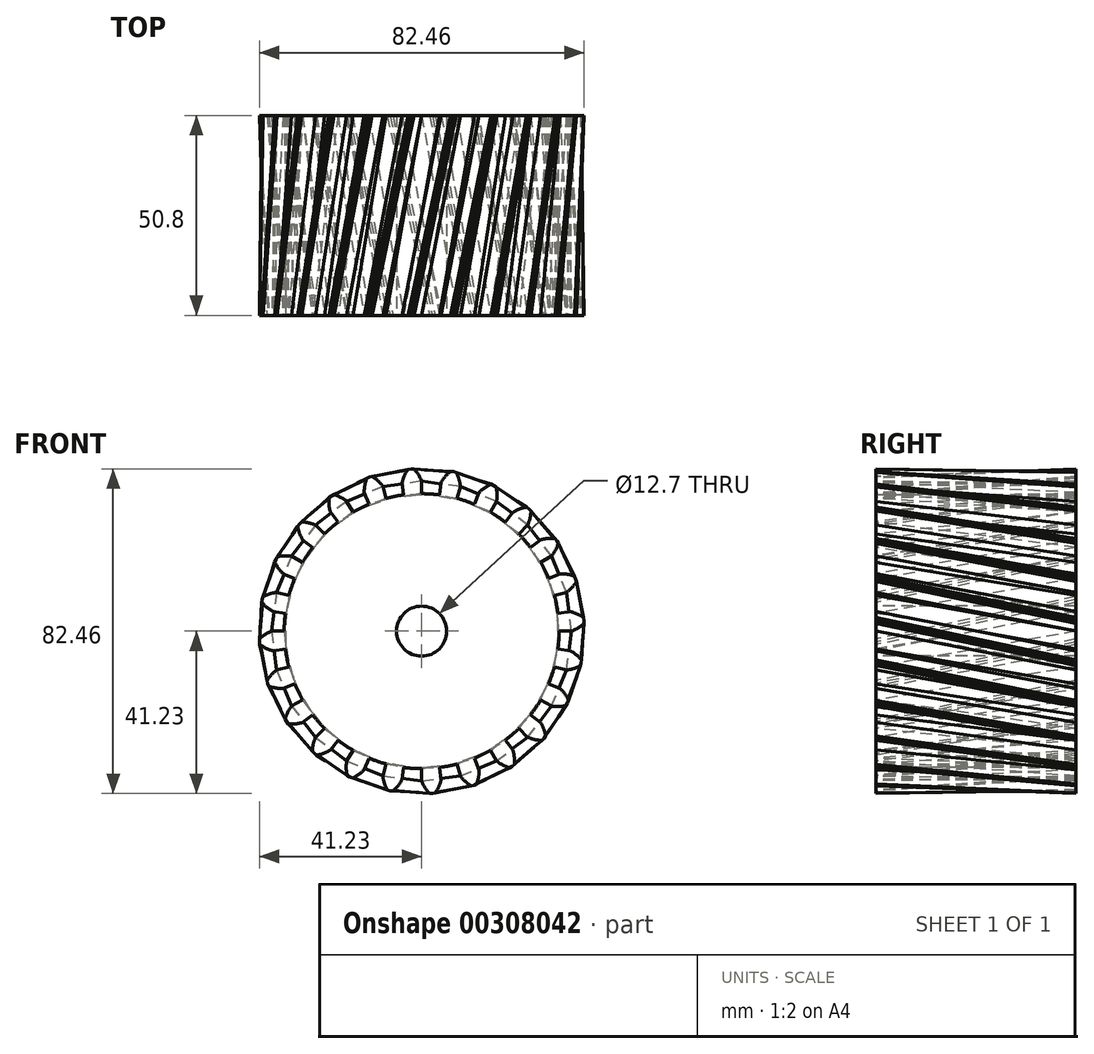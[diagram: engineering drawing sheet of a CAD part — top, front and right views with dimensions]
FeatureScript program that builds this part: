
annotation { "Feature Type Name" : "Feature", "Feature Type Description" : "" }
export const myFeature = defineFeature(function(context is Context, id is Id, definition is map)
    precondition{}
    {
        {
            var Q0;
            Q0=qCreatedBy(makeId("Front.planeOp"),FACE);
            var sketch = newSketch(context, id + "F0", { "sketchPlane" : qUnion([Q0])});
            skArc(sketch, "E0", {"start": v(-4.56, 34.63) * mm, "mid": v(-6.81, 34.25) * mm, "end": v(-9.04, 33.73) * mm});
            skArc(sketch, "E1.trimOffspring", {"start": v(0, 38.1) * mm, "mid": v(-0.83, 39.76) * mm, "end": v(-1.97, 41.23) * mm});
            skLineSegment(sketch, "E2", {"start": v(0, 38.1) * mm, "end": v(0, 34.93) * mm});
            skLineSegment(sketch, "E3", {"start": v(-1.97, 41.23) * mm, "end": v(-2.7, 41.23) * mm});
            skLineSegment(sketch, "E4.MirrorCS", {"start": v(-3.43, 41.13) * mm, "end": v(-2.7, 41.23) * mm});
            skArc(sketch, "E5.MirrorCS", {"start": v(-4.97, 37.77) * mm, "mid": v(-4.36, 39.53) * mm, "end": v(-3.43, 41.13) * mm});
            skLineSegment(sketch, "E6.MirrorCS", {"start": v(-4.97, 37.77) * mm, "end": v(-4.56, 34.63) * mm});
            skLineSegment(sketch, "E7.1.0", {"start": v(-14.58, 35.2) * mm, "end": v(-13.37, 32.27) * mm});
            skArc(sketch, "E7.1.1", {"start": v(-14.58, 35.2) * mm, "mid": v(-14.45, 37.05) * mm, "end": v(-13.96, 38.84) * mm});
            skLineSegment(sketch, "E7.1.2", {"start": v(-13.96, 38.84) * mm, "end": v(-13.28, 39.12) * mm});
            skLineSegment(sketch, "E7.1.3", {"start": v(-12.58, 39.31) * mm, "end": v(-13.28, 39.12) * mm});
            skLineSegment(sketch, "E7.1.4", {"start": v(-9.86, 36.8) * mm, "end": v(-9.04, 33.73) * mm});
            skArc(sketch, "E7.1.5", {"start": v(-9.86, 36.8) * mm, "mid": v(-11.1, 38.2) * mm, "end": v(-12.58, 39.31) * mm});
            skLineSegment(sketch, "E7.2.0", {"start": v(-23.2, 30.23) * mm, "end": v(-21.26, 27.7) * mm});
            skArc(sketch, "E7.2.1", {"start": v(-23.2, 30.23) * mm, "mid": v(-23.54, 32.05) * mm, "end": v(-23.53, 33.9) * mm});
            skLineSegment(sketch, "E7.2.2", {"start": v(-23.53, 33.9) * mm, "end": v(-22.95, 34.35) * mm});
            skLineSegment(sketch, "E7.2.3", {"start": v(-22.32, 34.72) * mm, "end": v(-22.95, 34.35) * mm});
            skLineSegment(sketch, "E7.2.4", {"start": v(-19.05, 33) * mm, "end": v(-17.46, 30.25) * mm});
            skArc(sketch, "E7.2.5", {"start": v(-19.05, 33) * mm, "mid": v(-20.6, 34.02) * mm, "end": v(-22.32, 34.72) * mm});
            skLineSegment(sketch, "E7.3.0", {"start": v(-30.23, 23.2) * mm, "end": v(-27.7, 21.26) * mm});
            skArc(sketch, "E7.3.1", {"start": v(-30.23, 23.2) * mm, "mid": v(-31.04, 24.87) * mm, "end": v(-31.5, 26.66) * mm});
            skLineSegment(sketch, "E7.3.2", {"start": v(-31.5, 26.66) * mm, "end": v(-31.06, 27.24) * mm});
            skLineSegment(sketch, "E7.3.3", {"start": v(-30.55, 27.76) * mm, "end": v(-31.06, 27.24) * mm});
            skLineSegment(sketch, "E7.3.4", {"start": v(-26.94, 26.94) * mm, "end": v(-24.7, 24.7) * mm});
            skArc(sketch, "E7.3.5", {"start": v(-26.94, 26.94) * mm, "mid": v(-28.7, 27.53) * mm, "end": v(-30.55, 27.76) * mm});
            skLineSegment(sketch, "E7.4.0", {"start": v(-35.2, 14.58) * mm, "end": v(-32.27, 13.37) * mm});
            skArc(sketch, "E7.4.1", {"start": v(-35.2, 14.58) * mm, "mid": v(-36.42, 15.99) * mm, "end": v(-37.33, 17.6) * mm});
            skLineSegment(sketch, "E7.4.2", {"start": v(-37.33, 17.6) * mm, "end": v(-37.06, 18.27) * mm});
            skLineSegment(sketch, "E7.4.3", {"start": v(-36.7, 18.9) * mm, "end": v(-37.06, 18.27) * mm});
            skLineSegment(sketch, "E7.4.4", {"start": v(-33, 19.05) * mm, "end": v(-30.25, 17.46) * mm});
            skArc(sketch, "E7.4.5", {"start": v(-33, 19.05) * mm, "mid": v(-34.85, 19.16) * mm, "end": v(-36.7, 18.9) * mm});
            skLineSegment(sketch, "E7.5.0", {"start": v(-37.77, 4.97) * mm, "end": v(-34.63, 4.56) * mm});
            skArc(sketch, "E7.5.1", {"start": v(-37.77, 4.97) * mm, "mid": v(-39.31, 6.02) * mm, "end": v(-40.62, 7.34) * mm});
            skLineSegment(sketch, "E7.5.2", {"start": v(-40.62, 7.34) * mm, "end": v(-40.52, 8.06) * mm});
            skLineSegment(sketch, "E7.5.3", {"start": v(-40.33, 8.77) * mm, "end": v(-40.52, 8.06) * mm});
            skLineSegment(sketch, "E7.5.4", {"start": v(-36.8, 9.86) * mm, "end": v(-33.73, 9.04) * mm});
            skArc(sketch, "E7.5.5", {"start": v(-36.8, 9.86) * mm, "mid": v(-38.62, 9.49) * mm, "end": v(-40.33, 8.77) * mm});
            skLineSegment(sketch, "E7.6.0", {"start": v(-37.77, -4.97) * mm, "end": v(-34.63, -4.56) * mm});
            skArc(sketch, "E7.6.1", {"start": v(-37.77, -4.97) * mm, "mid": v(-39.53, -4.36) * mm, "end": v(-41.13, -3.43) * mm});
            skLineSegment(sketch, "E7.6.2", {"start": v(-41.13, -3.43) * mm, "end": v(-41.23, -2.7) * mm});
            skLineSegment(sketch, "E7.6.3", {"start": v(-41.23, -1.97) * mm, "end": v(-41.23, -2.7) * mm});
            skLineSegment(sketch, "E7.6.4", {"start": v(-38.1, 0) * mm, "end": v(-34.93, 0) * mm});
            skArc(sketch, "E7.6.5", {"start": v(-38.1, 0) * mm, "mid": v(-39.76, -0.83) * mm, "end": v(-41.23, -1.97) * mm});
            skLineSegment(sketch, "E7.7.0", {"start": v(-35.2, -14.58) * mm, "end": v(-32.27, -13.37) * mm});
            skArc(sketch, "E7.7.1", {"start": v(-35.2, -14.58) * mm, "mid": v(-37.05, -14.45) * mm, "end": v(-38.84, -13.96) * mm});
            skLineSegment(sketch, "E7.7.2", {"start": v(-38.84, -13.96) * mm, "end": v(-39.12, -13.28) * mm});
            skLineSegment(sketch, "E7.7.3", {"start": v(-39.31, -12.58) * mm, "end": v(-39.12, -13.28) * mm});
            skLineSegment(sketch, "E7.7.4", {"start": v(-36.8, -9.86) * mm, "end": v(-33.73, -9.04) * mm});
            skArc(sketch, "E7.7.5", {"start": v(-36.8, -9.86) * mm, "mid": v(-38.2, -11.1) * mm, "end": v(-39.31, -12.58) * mm});
            skLineSegment(sketch, "E7.8.0", {"start": v(-30.23, -23.2) * mm, "end": v(-27.7, -21.26) * mm});
            skArc(sketch, "E7.8.1", {"start": v(-30.23, -23.2) * mm, "mid": v(-32.05, -23.54) * mm, "end": v(-33.9, -23.53) * mm});
            skLineSegment(sketch, "E7.8.2", {"start": v(-33.9, -23.53) * mm, "end": v(-34.35, -22.95) * mm});
            skLineSegment(sketch, "E7.8.3", {"start": v(-34.72, -22.32) * mm, "end": v(-34.35, -22.95) * mm});
            skLineSegment(sketch, "E7.8.4", {"start": v(-33, -19.05) * mm, "end": v(-30.25, -17.46) * mm});
            skArc(sketch, "E7.8.5", {"start": v(-33, -19.05) * mm, "mid": v(-34.02, -20.6) * mm, "end": v(-34.72, -22.32) * mm});
            skLineSegment(sketch, "E7.9.0", {"start": v(-23.2, -30.23) * mm, "end": v(-21.26, -27.7) * mm});
            skArc(sketch, "E7.9.1", {"start": v(-23.2, -30.23) * mm, "mid": v(-24.87, -31.04) * mm, "end": v(-26.66, -31.5) * mm});
            skLineSegment(sketch, "E7.9.2", {"start": v(-26.66, -31.5) * mm, "end": v(-27.24, -31.06) * mm});
            skLineSegment(sketch, "E7.9.3", {"start": v(-27.76, -30.55) * mm, "end": v(-27.24, -31.06) * mm});
            skLineSegment(sketch, "E7.9.4", {"start": v(-26.94, -26.94) * mm, "end": v(-24.7, -24.7) * mm});
            skArc(sketch, "E7.9.5", {"start": v(-26.94, -26.94) * mm, "mid": v(-27.53, -28.7) * mm, "end": v(-27.76, -30.55) * mm});
            skLineSegment(sketch, "E7.10.0", {"start": v(-14.58, -35.2) * mm, "end": v(-13.37, -32.27) * mm});
            skArc(sketch, "E7.10.1", {"start": v(-14.58, -35.2) * mm, "mid": v(-15.99, -36.42) * mm, "end": v(-17.6, -37.33) * mm});
            skLineSegment(sketch, "E7.10.2", {"start": v(-17.6, -37.33) * mm, "end": v(-18.27, -37.06) * mm});
            skLineSegment(sketch, "E7.10.3", {"start": v(-18.9, -36.7) * mm, "end": v(-18.27, -37.06) * mm});
            skLineSegment(sketch, "E7.10.4", {"start": v(-19.05, -33) * mm, "end": v(-17.46, -30.25) * mm});
            skArc(sketch, "E7.10.5", {"start": v(-19.05, -33) * mm, "mid": v(-19.16, -34.85) * mm, "end": v(-18.9, -36.7) * mm});
            skLineSegment(sketch, "E7.11.0", {"start": v(-4.97, -37.77) * mm, "end": v(-4.56, -34.63) * mm});
            skArc(sketch, "E7.11.1", {"start": v(-4.97, -37.77) * mm, "mid": v(-6.02, -39.31) * mm, "end": v(-7.34, -40.62) * mm});
            skLineSegment(sketch, "E7.11.2", {"start": v(-7.34, -40.62) * mm, "end": v(-8.06, -40.52) * mm});
            skLineSegment(sketch, "E7.11.3", {"start": v(-8.77, -40.33) * mm, "end": v(-8.06, -40.52) * mm});
            skLineSegment(sketch, "E7.11.4", {"start": v(-9.86, -36.8) * mm, "end": v(-9.04, -33.73) * mm});
            skArc(sketch, "E7.11.5", {"start": v(-9.86, -36.8) * mm, "mid": v(-9.49, -38.62) * mm, "end": v(-8.77, -40.33) * mm});
            skLineSegment(sketch, "E7.12.0", {"start": v(4.97, -37.77) * mm, "end": v(4.56, -34.63) * mm});
            skArc(sketch, "E7.12.1", {"start": v(4.97, -37.77) * mm, "mid": v(4.36, -39.53) * mm, "end": v(3.43, -41.13) * mm});
            skLineSegment(sketch, "E7.12.2", {"start": v(3.43, -41.13) * mm, "end": v(2.7, -41.23) * mm});
            skLineSegment(sketch, "E7.12.3", {"start": v(1.97, -41.23) * mm, "end": v(2.7, -41.23) * mm});
            skLineSegment(sketch, "E7.12.4", {"start": v(0, -38.1) * mm, "end": v(0, -34.93) * mm});
            skArc(sketch, "E7.12.5", {"start": v(0, -38.1) * mm, "mid": v(0.83, -39.76) * mm, "end": v(1.97, -41.23) * mm});
            skLineSegment(sketch, "E7.13.0", {"start": v(14.58, -35.2) * mm, "end": v(13.37, -32.27) * mm});
            skArc(sketch, "E7.13.1", {"start": v(14.58, -35.2) * mm, "mid": v(14.45, -37.05) * mm, "end": v(13.96, -38.84) * mm});
            skLineSegment(sketch, "E7.13.2", {"start": v(13.96, -38.84) * mm, "end": v(13.28, -39.12) * mm});
            skLineSegment(sketch, "E7.13.3", {"start": v(12.58, -39.31) * mm, "end": v(13.28, -39.12) * mm});
            skLineSegment(sketch, "E7.13.4", {"start": v(9.86, -36.8) * mm, "end": v(9.04, -33.73) * mm});
            skArc(sketch, "E7.13.5", {"start": v(9.86, -36.8) * mm, "mid": v(11.1, -38.2) * mm, "end": v(12.58, -39.31) * mm});
            skLineSegment(sketch, "E7.14.0", {"start": v(23.2, -30.23) * mm, "end": v(21.26, -27.7) * mm});
            skArc(sketch, "E7.14.1", {"start": v(23.2, -30.23) * mm, "mid": v(23.54, -32.05) * mm, "end": v(23.53, -33.9) * mm});
            skLineSegment(sketch, "E7.14.2", {"start": v(23.53, -33.9) * mm, "end": v(22.95, -34.35) * mm});
            skLineSegment(sketch, "E7.14.3", {"start": v(22.32, -34.72) * mm, "end": v(22.95, -34.35) * mm});
            skLineSegment(sketch, "E7.14.4", {"start": v(19.05, -33) * mm, "end": v(17.46, -30.25) * mm});
            skArc(sketch, "E7.14.5", {"start": v(19.05, -33) * mm, "mid": v(20.6, -34.02) * mm, "end": v(22.32, -34.72) * mm});
            skLineSegment(sketch, "E7.15.0", {"start": v(30.23, -23.2) * mm, "end": v(27.7, -21.26) * mm});
            skArc(sketch, "E7.15.1", {"start": v(30.23, -23.2) * mm, "mid": v(31.04, -24.87) * mm, "end": v(31.5, -26.66) * mm});
            skLineSegment(sketch, "E7.15.2", {"start": v(31.5, -26.66) * mm, "end": v(31.06, -27.24) * mm});
            skLineSegment(sketch, "E7.15.3", {"start": v(30.55, -27.76) * mm, "end": v(31.06, -27.24) * mm});
            skLineSegment(sketch, "E7.15.4", {"start": v(26.94, -26.94) * mm, "end": v(24.7, -24.7) * mm});
            skArc(sketch, "E7.15.5", {"start": v(26.94, -26.94) * mm, "mid": v(28.7, -27.53) * mm, "end": v(30.55, -27.76) * mm});
            skLineSegment(sketch, "E7.16.0", {"start": v(35.2, -14.58) * mm, "end": v(32.27, -13.37) * mm});
            skArc(sketch, "E7.16.1", {"start": v(35.2, -14.58) * mm, "mid": v(36.42, -15.99) * mm, "end": v(37.33, -17.6) * mm});
            skLineSegment(sketch, "E7.16.2", {"start": v(37.33, -17.6) * mm, "end": v(37.06, -18.27) * mm});
            skLineSegment(sketch, "E7.16.3", {"start": v(36.7, -18.9) * mm, "end": v(37.06, -18.27) * mm});
            skLineSegment(sketch, "E7.16.4", {"start": v(33, -19.05) * mm, "end": v(30.25, -17.46) * mm});
            skArc(sketch, "E7.16.5", {"start": v(33, -19.05) * mm, "mid": v(34.85, -19.16) * mm, "end": v(36.7, -18.9) * mm});
            skLineSegment(sketch, "E7.17.0", {"start": v(37.77, -4.97) * mm, "end": v(34.63, -4.56) * mm});
            skArc(sketch, "E7.17.1", {"start": v(37.77, -4.97) * mm, "mid": v(39.31, -6.02) * mm, "end": v(40.62, -7.34) * mm});
            skLineSegment(sketch, "E7.17.2", {"start": v(40.62, -7.34) * mm, "end": v(40.52, -8.06) * mm});
            skLineSegment(sketch, "E7.17.3", {"start": v(40.33, -8.77) * mm, "end": v(40.52, -8.06) * mm});
            skLineSegment(sketch, "E7.17.4", {"start": v(36.8, -9.86) * mm, "end": v(33.73, -9.04) * mm});
            skArc(sketch, "E7.17.5", {"start": v(36.8, -9.86) * mm, "mid": v(38.62, -9.49) * mm, "end": v(40.33, -8.77) * mm});
            skLineSegment(sketch, "E7.18.0", {"start": v(37.77, 4.97) * mm, "end": v(34.63, 4.56) * mm});
            skArc(sketch, "E7.18.1", {"start": v(37.77, 4.97) * mm, "mid": v(39.53, 4.36) * mm, "end": v(41.13, 3.43) * mm});
            skLineSegment(sketch, "E7.18.2", {"start": v(41.13, 3.43) * mm, "end": v(41.23, 2.7) * mm});
            skLineSegment(sketch, "E7.18.3", {"start": v(41.23, 1.97) * mm, "end": v(41.23, 2.7) * mm});
            skLineSegment(sketch, "E7.18.4", {"start": v(38.1, 0) * mm, "end": v(34.93, 0) * mm});
            skArc(sketch, "E7.18.5", {"start": v(38.1, 0) * mm, "mid": v(39.76, 0.83) * mm, "end": v(41.23, 1.97) * mm});
            skLineSegment(sketch, "E7.19.0", {"start": v(35.2, 14.58) * mm, "end": v(32.27, 13.37) * mm});
            skArc(sketch, "E7.19.1", {"start": v(35.2, 14.58) * mm, "mid": v(37.05, 14.45) * mm, "end": v(38.84, 13.96) * mm});
            skLineSegment(sketch, "E7.19.2", {"start": v(38.84, 13.96) * mm, "end": v(39.12, 13.28) * mm});
            skLineSegment(sketch, "E7.19.3", {"start": v(39.31, 12.58) * mm, "end": v(39.12, 13.28) * mm});
            skLineSegment(sketch, "E7.19.4", {"start": v(36.8, 9.86) * mm, "end": v(33.73, 9.04) * mm});
            skArc(sketch, "E7.19.5", {"start": v(36.8, 9.86) * mm, "mid": v(38.2, 11.1) * mm, "end": v(39.31, 12.58) * mm});
            skLineSegment(sketch, "E7.20.0", {"start": v(30.23, 23.2) * mm, "end": v(27.7, 21.26) * mm});
            skArc(sketch, "E7.20.1", {"start": v(30.23, 23.2) * mm, "mid": v(32.05, 23.54) * mm, "end": v(33.9, 23.53) * mm});
            skLineSegment(sketch, "E7.20.2", {"start": v(33.9, 23.53) * mm, "end": v(34.35, 22.95) * mm});
            skLineSegment(sketch, "E7.20.3", {"start": v(34.72, 22.32) * mm, "end": v(34.35, 22.95) * mm});
            skLineSegment(sketch, "E7.20.4", {"start": v(33, 19.05) * mm, "end": v(30.25, 17.46) * mm});
            skArc(sketch, "E7.20.5", {"start": v(33, 19.05) * mm, "mid": v(34.02, 20.6) * mm, "end": v(34.72, 22.32) * mm});
            skLineSegment(sketch, "E7.21.0", {"start": v(23.2, 30.23) * mm, "end": v(21.26, 27.7) * mm});
            skArc(sketch, "E7.21.1", {"start": v(23.2, 30.23) * mm, "mid": v(24.87, 31.04) * mm, "end": v(26.66, 31.5) * mm});
            skLineSegment(sketch, "E7.21.2", {"start": v(26.66, 31.5) * mm, "end": v(27.24, 31.06) * mm});
            skLineSegment(sketch, "E7.21.3", {"start": v(27.76, 30.55) * mm, "end": v(27.24, 31.06) * mm});
            skLineSegment(sketch, "E7.21.4", {"start": v(26.94, 26.94) * mm, "end": v(24.7, 24.7) * mm});
            skArc(sketch, "E7.21.5", {"start": v(26.94, 26.94) * mm, "mid": v(27.53, 28.7) * mm, "end": v(27.76, 30.55) * mm});
            skLineSegment(sketch, "E7.22.0", {"start": v(14.58, 35.2) * mm, "end": v(13.37, 32.27) * mm});
            skArc(sketch, "E7.22.1", {"start": v(14.58, 35.2) * mm, "mid": v(15.99, 36.42) * mm, "end": v(17.6, 37.33) * mm});
            skLineSegment(sketch, "E7.22.2", {"start": v(17.6, 37.33) * mm, "end": v(18.27, 37.06) * mm});
            skLineSegment(sketch, "E7.22.3", {"start": v(18.9, 36.7) * mm, "end": v(18.27, 37.06) * mm});
            skLineSegment(sketch, "E7.22.4", {"start": v(19.05, 33) * mm, "end": v(17.46, 30.25) * mm});
            skArc(sketch, "E7.22.5", {"start": v(19.05, 33) * mm, "mid": v(19.16, 34.85) * mm, "end": v(18.9, 36.7) * mm});
            skLineSegment(sketch, "E7.23.0", {"start": v(4.97, 37.77) * mm, "end": v(4.56, 34.63) * mm});
            skArc(sketch, "E7.23.1", {"start": v(4.97, 37.77) * mm, "mid": v(6.02, 39.31) * mm, "end": v(7.34, 40.62) * mm});
            skLineSegment(sketch, "E7.23.2", {"start": v(7.34, 40.62) * mm, "end": v(8.06, 40.52) * mm});
            skLineSegment(sketch, "E7.23.3", {"start": v(8.77, 40.33) * mm, "end": v(8.06, 40.52) * mm});
            skLineSegment(sketch, "E7.23.4", {"start": v(9.86, 36.8) * mm, "end": v(9.04, 33.73) * mm});
            skArc(sketch, "E7.23.5", {"start": v(9.86, 36.8) * mm, "mid": v(9.49, 38.62) * mm, "end": v(8.77, 40.33) * mm});
            skArc(sketch, "E8.trimOffspring", {"start": v(4.56, 34.63) * mm, "mid": v(2.28, 34.85) * mm, "end": v(0, 34.92) * mm});
            skArc(sketch, "E9.trimOffspring", {"start": v(-13.37, 32.27) * mm, "mid": v(-15.45, 31.32) * mm, "end": v(-17.46, 30.25) * mm});
            skArc(sketch, "E10.trimOffspring", {"start": v(-21.26, 27.7) * mm, "mid": v(-23.03, 26.26) * mm, "end": v(-24.7, 24.7) * mm});
            skArc(sketch, "E11.trimOffspring", {"start": v(13.37, 32.27) * mm, "mid": v(11.23, 33.07) * mm, "end": v(9.04, 33.73) * mm});
            skArc(sketch, "E12.trimOffspring", {"start": v(-4.56, -34.63) * mm, "mid": v(-2.28, -34.85) * mm, "end": v(0, -34.93) * mm});
            skArc(sketch, "E13.trimOffspring", {"start": v(-13.37, -32.27) * mm, "mid": v(-11.23, -33.07) * mm, "end": v(-9.04, -33.73) * mm});
            skArc(sketch, "E14.trimOffspring", {"start": v(4.56, -34.63) * mm, "mid": v(6.81, -34.25) * mm, "end": v(9.04, -33.73) * mm});
            skArc(sketch, "E15.trimOffspring", {"start": v(13.37, -32.27) * mm, "mid": v(15.45, -31.32) * mm, "end": v(17.46, -30.25) * mm});
            skArc(sketch, "E16.trimOffspring", {"start": v(21.26, -27.7) * mm, "mid": v(23.03, -26.26) * mm, "end": v(24.7, -24.7) * mm});
            skArc(sketch, "E17.trimOffspring", {"start": v(27.7, -21.26) * mm, "mid": v(29.04, -19.4) * mm, "end": v(30.25, -17.46) * mm});
            skArc(sketch, "E18.trimOffspring", {"start": v(32.27, -13.37) * mm, "mid": v(33.07, -11.23) * mm, "end": v(33.73, -9.04) * mm});
            skArc(sketch, "E19.trimOffspring", {"start": v(34.63, -4.56) * mm, "mid": v(34.85, -2.28) * mm, "end": v(34.93, 0) * mm});
            skArc(sketch, "E20.trimOffspring", {"start": v(-21.26, -27.7) * mm, "mid": v(-19.4, -29.04) * mm, "end": v(-17.46, -30.25) * mm});
            skArc(sketch, "E21.trimOffspring", {"start": v(-27.7, -21.26) * mm, "mid": v(-26.26, -23.03) * mm, "end": v(-24.7, -24.7) * mm});
            skArc(sketch, "E22.trimOffspring", {"start": v(-32.27, -13.37) * mm, "mid": v(-31.32, -15.45) * mm, "end": v(-30.25, -17.46) * mm});
            skArc(sketch, "E23.trimOffspring", {"start": v(-34.63, -4.56) * mm, "mid": v(-34.25, -6.81) * mm, "end": v(-33.73, -9.04) * mm});
            skArc(sketch, "E24.trimOffspring", {"start": v(-34.63, 4.56) * mm, "mid": v(-34.85, 2.28) * mm, "end": v(-34.93, 0) * mm});
            skArc(sketch, "E25.trimOffspring", {"start": v(-32.27, 13.37) * mm, "mid": v(-33.07, 11.23) * mm, "end": v(-33.73, 9.04) * mm});
            skArc(sketch, "E26.trimOffspring", {"start": v(21.26, 27.7) * mm, "mid": v(19.4, 29.04) * mm, "end": v(17.46, 30.25) * mm});
            skArc(sketch, "E27.trimOffspring", {"start": v(34.63, 4.56) * mm, "mid": v(34.25, 6.81) * mm, "end": v(33.73, 9.04) * mm});
            skArc(sketch, "E28.trimOffspring", {"start": v(32.27, 13.37) * mm, "mid": v(31.32, 15.45) * mm, "end": v(30.25, 17.46) * mm});
            skArc(sketch, "E29.trimOffspring", {"start": v(27.7, 21.26) * mm, "mid": v(26.26, 23.03) * mm, "end": v(24.7, 24.7) * mm});
            skArc(sketch, "E30.trimOffspring", {"start": v(-27.7, 21.26) * mm, "mid": v(-29.04, 19.4) * mm, "end": v(-30.25, 17.46) * mm});
            skSolve(sketch);
        }
        {
            var Q0;
            Q0=makeQuery(id+"F0.imprint","IMPRINT",FACE,{"disambiguationData":[TD([[makeQuery(id+"F0.imprint","IMPRINT",EDGE,{"derivedFrom":sQuery(id+"F0.wireOp",EDGE,"E0")}),1.0]])]});
            cPlane(context, id + "F1", {"entities" : qUnion([Q0]), "cplaneType" : CPlaneType.OFFSET, "offset" : 50.8 * mm, "width" : 152.4 * mm, "height" : 152.4 * mm});
        }
        {
            var Q0;
            Q0=qCreatedBy(id+"F1.planeOp",FACE);
            var sketch = newSketch(context, id + "F2", { "sketchPlane" : qUnion([Q0])});
            skLineSegment(sketch, "E31.0.0", {"start": v(-30.25, -17.46) * mm, "end": v(-33, -19.05) * mm});
            skArc(sketch, "E31.0.1", {"start": v(-33, -19.05) * mm, "mid": v(-34.02, -20.6) * mm, "end": v(-34.72, -22.32) * mm});
            skLineSegment(sketch, "E31.0.2", {"start": v(-34.72, -22.32) * mm, "end": v(-34.35, -22.95) * mm});
            skLineSegment(sketch, "E31.0.3", {"start": v(-34.35, -22.95) * mm, "end": v(-33.9, -23.53) * mm});
            skArc(sketch, "E31.0.4", {"start": v(-33.9, -23.53) * mm, "mid": v(-32.05, -23.54) * mm, "end": v(-30.23, -23.2) * mm});
            skLineSegment(sketch, "E31.0.5", {"start": v(-30.23, -23.2) * mm, "end": v(-27.7, -21.26) * mm});
            skArc(sketch, "E31.0.6", {"start": v(-27.7, -21.26) * mm, "mid": v(-26.26, -23.03) * mm, "end": v(-24.7, -24.7) * mm});
            skLineSegment(sketch, "E31.0.7", {"start": v(-24.7, -24.7) * mm, "end": v(-26.94, -26.94) * mm});
            skArc(sketch, "E31.0.8", {"start": v(-26.94, -26.94) * mm, "mid": v(-27.53, -28.7) * mm, "end": v(-27.76, -30.55) * mm});
            skLineSegment(sketch, "E31.0.9", {"start": v(-27.76, -30.55) * mm, "end": v(-27.24, -31.06) * mm});
            skLineSegment(sketch, "E31.0.10", {"start": v(-27.24, -31.06) * mm, "end": v(-26.66, -31.5) * mm});
            skArc(sketch, "E31.0.11", {"start": v(-26.66, -31.5) * mm, "mid": v(-24.87, -31.04) * mm, "end": v(-23.2, -30.23) * mm});
            skLineSegment(sketch, "E31.0.12", {"start": v(-23.2, -30.23) * mm, "end": v(-21.26, -27.7) * mm});
            skArc(sketch, "E31.0.13", {"start": v(-21.26, -27.7) * mm, "mid": v(-19.4, -29.04) * mm, "end": v(-17.46, -30.25) * mm});
            skLineSegment(sketch, "E31.0.14", {"start": v(-17.46, -30.25) * mm, "end": v(-19.05, -33) * mm});
            skArc(sketch, "E31.0.15", {"start": v(-19.05, -33) * mm, "mid": v(-19.16, -34.85) * mm, "end": v(-18.9, -36.7) * mm});
            skLineSegment(sketch, "E31.0.16", {"start": v(-18.9, -36.7) * mm, "end": v(-18.27, -37.06) * mm});
            skLineSegment(sketch, "E31.0.17", {"start": v(-18.27, -37.06) * mm, "end": v(-17.6, -37.33) * mm});
            skArc(sketch, "E31.0.18", {"start": v(-17.6, -37.33) * mm, "mid": v(-15.99, -36.42) * mm, "end": v(-14.58, -35.2) * mm});
            skLineSegment(sketch, "E31.0.19", {"start": v(-14.58, -35.2) * mm, "end": v(-13.37, -32.27) * mm});
            skArc(sketch, "E31.0.20", {"start": v(-13.37, -32.27) * mm, "mid": v(-11.23, -33.07) * mm, "end": v(-9.04, -33.73) * mm});
            skLineSegment(sketch, "E31.0.21", {"start": v(-9.04, -33.73) * mm, "end": v(-9.86, -36.8) * mm});
            skArc(sketch, "E31.0.22", {"start": v(-9.86, -36.8) * mm, "mid": v(-9.49, -38.62) * mm, "end": v(-8.77, -40.33) * mm});
            skLineSegment(sketch, "E31.0.23", {"start": v(-8.77, -40.33) * mm, "end": v(-8.06, -40.52) * mm});
            skLineSegment(sketch, "E31.0.24", {"start": v(-8.06, -40.52) * mm, "end": v(-7.34, -40.62) * mm});
            skArc(sketch, "E31.0.25", {"start": v(-7.34, -40.62) * mm, "mid": v(-6.02, -39.31) * mm, "end": v(-4.97, -37.77) * mm});
            skLineSegment(sketch, "E31.0.26", {"start": v(-4.97, -37.77) * mm, "end": v(-4.56, -34.63) * mm});
            skArc(sketch, "E31.0.27", {"start": v(-4.56, -34.63) * mm, "mid": v(-2.28, -34.85) * mm, "end": v(0, -34.93) * mm});
            skLineSegment(sketch, "E31.0.28", {"start": v(0, -34.93) * mm, "end": v(0, -38.1) * mm});
            skArc(sketch, "E31.0.29", {"start": v(0, -38.1) * mm, "mid": v(0.83, -39.76) * mm, "end": v(1.97, -41.23) * mm});
            skLineSegment(sketch, "E31.0.30", {"start": v(1.97, -41.23) * mm, "end": v(2.7, -41.23) * mm});
            skLineSegment(sketch, "E31.0.31", {"start": v(2.7, -41.23) * mm, "end": v(3.43, -41.13) * mm});
            skArc(sketch, "E31.0.32", {"start": v(3.43, -41.13) * mm, "mid": v(4.36, -39.53) * mm, "end": v(4.97, -37.77) * mm});
            skLineSegment(sketch, "E31.0.33", {"start": v(4.97, -37.77) * mm, "end": v(4.56, -34.63) * mm});
            skArc(sketch, "E31.0.34", {"start": v(4.56, -34.63) * mm, "mid": v(6.81, -34.25) * mm, "end": v(9.04, -33.73) * mm});
            skLineSegment(sketch, "E31.0.35", {"start": v(9.04, -33.73) * mm, "end": v(9.86, -36.8) * mm});
            skArc(sketch, "E31.0.36", {"start": v(9.86, -36.8) * mm, "mid": v(11.1, -38.2) * mm, "end": v(12.58, -39.31) * mm});
            skLineSegment(sketch, "E31.0.37", {"start": v(12.58, -39.31) * mm, "end": v(13.28, -39.12) * mm});
            skLineSegment(sketch, "E31.0.38", {"start": v(13.28, -39.12) * mm, "end": v(13.96, -38.84) * mm});
            skArc(sketch, "E31.0.39", {"start": v(13.96, -38.84) * mm, "mid": v(14.45, -37.05) * mm, "end": v(14.58, -35.2) * mm});
            skLineSegment(sketch, "E31.0.40", {"start": v(14.58, -35.2) * mm, "end": v(13.37, -32.27) * mm});
            skArc(sketch, "E31.0.41", {"start": v(13.37, -32.27) * mm, "mid": v(15.45, -31.32) * mm, "end": v(17.46, -30.25) * mm});
            skLineSegment(sketch, "E31.0.42", {"start": v(17.46, -30.25) * mm, "end": v(19.05, -33) * mm});
            skArc(sketch, "E31.0.43", {"start": v(19.05, -33) * mm, "mid": v(20.6, -34.02) * mm, "end": v(22.32, -34.72) * mm});
            skLineSegment(sketch, "E31.0.44", {"start": v(22.32, -34.72) * mm, "end": v(22.95, -34.35) * mm});
            skLineSegment(sketch, "E31.0.45", {"start": v(22.95, -34.35) * mm, "end": v(23.53, -33.9) * mm});
            skArc(sketch, "E31.0.46", {"start": v(23.53, -33.9) * mm, "mid": v(23.54, -32.05) * mm, "end": v(23.2, -30.23) * mm});
            skLineSegment(sketch, "E31.0.47", {"start": v(23.2, -30.23) * mm, "end": v(21.26, -27.7) * mm});
            skArc(sketch, "E31.0.48", {"start": v(21.26, -27.7) * mm, "mid": v(23.03, -26.26) * mm, "end": v(24.7, -24.7) * mm});
            skLineSegment(sketch, "E31.0.49", {"start": v(24.7, -24.7) * mm, "end": v(26.94, -26.94) * mm});
            skArc(sketch, "E31.0.50", {"start": v(26.94, -26.94) * mm, "mid": v(28.7, -27.53) * mm, "end": v(30.55, -27.76) * mm});
            skLineSegment(sketch, "E31.0.51", {"start": v(30.55, -27.76) * mm, "end": v(31.06, -27.24) * mm});
            skLineSegment(sketch, "E31.0.52", {"start": v(31.06, -27.24) * mm, "end": v(31.5, -26.66) * mm});
            skArc(sketch, "E31.0.53", {"start": v(31.5, -26.66) * mm, "mid": v(31.04, -24.87) * mm, "end": v(30.23, -23.2) * mm});
            skLineSegment(sketch, "E31.0.54", {"start": v(30.23, -23.2) * mm, "end": v(27.7, -21.26) * mm});
            skArc(sketch, "E31.0.55", {"start": v(27.7, -21.26) * mm, "mid": v(29.04, -19.4) * mm, "end": v(30.25, -17.46) * mm});
            skLineSegment(sketch, "E31.0.56", {"start": v(30.25, -17.46) * mm, "end": v(33, -19.05) * mm});
            skArc(sketch, "E31.0.57", {"start": v(33, -19.05) * mm, "mid": v(34.85, -19.16) * mm, "end": v(36.7, -18.9) * mm});
            skLineSegment(sketch, "E31.0.58", {"start": v(36.7, -18.9) * mm, "end": v(37.06, -18.27) * mm});
            skLineSegment(sketch, "E31.0.59", {"start": v(37.06, -18.27) * mm, "end": v(37.33, -17.6) * mm});
            skArc(sketch, "E31.0.60", {"start": v(37.33, -17.6) * mm, "mid": v(36.42, -15.99) * mm, "end": v(35.2, -14.58) * mm});
            skLineSegment(sketch, "E31.0.61", {"start": v(35.2, -14.58) * mm, "end": v(32.27, -13.37) * mm});
            skArc(sketch, "E31.0.62", {"start": v(32.27, -13.37) * mm, "mid": v(33.07, -11.23) * mm, "end": v(33.73, -9.04) * mm});
            skLineSegment(sketch, "E31.0.63", {"start": v(33.73, -9.04) * mm, "end": v(36.8, -9.86) * mm});
            skArc(sketch, "E31.0.64", {"start": v(36.8, -9.86) * mm, "mid": v(38.62, -9.49) * mm, "end": v(40.33, -8.77) * mm});
            skLineSegment(sketch, "E31.0.65", {"start": v(40.33, -8.77) * mm, "end": v(40.52, -8.06) * mm});
            skLineSegment(sketch, "E31.0.66", {"start": v(40.52, -8.06) * mm, "end": v(40.62, -7.34) * mm});
            skArc(sketch, "E31.0.67", {"start": v(40.62, -7.34) * mm, "mid": v(39.31, -6.02) * mm, "end": v(37.77, -4.97) * mm});
            skLineSegment(sketch, "E31.0.68", {"start": v(37.77, -4.97) * mm, "end": v(34.63, -4.56) * mm});
            skArc(sketch, "E31.0.69", {"start": v(34.63, -4.56) * mm, "mid": v(34.85, -2.28) * mm, "end": v(34.93, 0) * mm});
            skLineSegment(sketch, "E31.0.70", {"start": v(34.93, 0) * mm, "end": v(38.1, 0) * mm});
            skArc(sketch, "E31.0.71", {"start": v(38.1, 0) * mm, "mid": v(39.76, 0.83) * mm, "end": v(41.23, 1.97) * mm});
            skLineSegment(sketch, "E31.0.72", {"start": v(41.23, 1.97) * mm, "end": v(41.23, 2.7) * mm});
            skLineSegment(sketch, "E31.0.73", {"start": v(41.23, 2.7) * mm, "end": v(41.13, 3.43) * mm});
            skArc(sketch, "E31.0.74", {"start": v(41.13, 3.43) * mm, "mid": v(39.53, 4.36) * mm, "end": v(37.77, 4.97) * mm});
            skLineSegment(sketch, "E31.0.75", {"start": v(37.77, 4.97) * mm, "end": v(34.63, 4.56) * mm});
            skArc(sketch, "E31.0.76", {"start": v(34.63, 4.56) * mm, "mid": v(34.25, 6.81) * mm, "end": v(33.73, 9.04) * mm});
            skLineSegment(sketch, "E31.0.77", {"start": v(33.73, 9.04) * mm, "end": v(36.8, 9.86) * mm});
            skArc(sketch, "E31.0.78", {"start": v(36.8, 9.86) * mm, "mid": v(38.2, 11.1) * mm, "end": v(39.31, 12.58) * mm});
            skLineSegment(sketch, "E31.0.79", {"start": v(39.31, 12.58) * mm, "end": v(39.12, 13.28) * mm});
            skLineSegment(sketch, "E31.0.80", {"start": v(39.12, 13.28) * mm, "end": v(38.84, 13.96) * mm});
            skArc(sketch, "E31.0.81", {"start": v(38.84, 13.96) * mm, "mid": v(37.05, 14.45) * mm, "end": v(35.2, 14.58) * mm});
            skLineSegment(sketch, "E31.0.82", {"start": v(35.2, 14.58) * mm, "end": v(32.27, 13.37) * mm});
            skArc(sketch, "E31.0.83", {"start": v(32.27, 13.37) * mm, "mid": v(31.32, 15.45) * mm, "end": v(30.25, 17.46) * mm});
            skLineSegment(sketch, "E31.0.84", {"start": v(30.25, 17.46) * mm, "end": v(33, 19.05) * mm});
            skArc(sketch, "E31.0.85", {"start": v(33, 19.05) * mm, "mid": v(34.02, 20.6) * mm, "end": v(34.72, 22.32) * mm});
            skLineSegment(sketch, "E31.0.86", {"start": v(34.72, 22.32) * mm, "end": v(34.35, 22.95) * mm});
            skLineSegment(sketch, "E31.0.87", {"start": v(34.35, 22.95) * mm, "end": v(33.9, 23.53) * mm});
            skArc(sketch, "E31.0.88", {"start": v(33.9, 23.53) * mm, "mid": v(32.05, 23.54) * mm, "end": v(30.23, 23.2) * mm});
            skLineSegment(sketch, "E31.0.89", {"start": v(30.23, 23.2) * mm, "end": v(27.7, 21.26) * mm});
            skArc(sketch, "E31.0.90", {"start": v(27.7, 21.26) * mm, "mid": v(26.26, 23.03) * mm, "end": v(24.7, 24.7) * mm});
            skLineSegment(sketch, "E31.0.91", {"start": v(24.7, 24.7) * mm, "end": v(26.94, 26.94) * mm});
            skArc(sketch, "E31.0.92", {"start": v(26.94, 26.94) * mm, "mid": v(27.53, 28.7) * mm, "end": v(27.76, 30.55) * mm});
            skLineSegment(sketch, "E31.0.93", {"start": v(27.76, 30.55) * mm, "end": v(27.24, 31.06) * mm});
            skLineSegment(sketch, "E31.0.94", {"start": v(27.24, 31.06) * mm, "end": v(26.66, 31.5) * mm});
            skArc(sketch, "E31.0.95", {"start": v(26.66, 31.5) * mm, "mid": v(24.87, 31.04) * mm, "end": v(23.2, 30.23) * mm});
            skLineSegment(sketch, "E31.0.96", {"start": v(23.2, 30.23) * mm, "end": v(21.26, 27.7) * mm});
            skArc(sketch, "E31.0.97", {"start": v(21.26, 27.7) * mm, "mid": v(19.4, 29.04) * mm, "end": v(17.46, 30.25) * mm});
            skLineSegment(sketch, "E31.0.98", {"start": v(17.46, 30.25) * mm, "end": v(19.05, 33) * mm});
            skArc(sketch, "E31.0.99", {"start": v(19.05, 33) * mm, "mid": v(19.16, 34.85) * mm, "end": v(18.9, 36.7) * mm});
            skLineSegment(sketch, "E31.0.100", {"start": v(18.9, 36.7) * mm, "end": v(18.27, 37.06) * mm});
            skLineSegment(sketch, "E31.0.101", {"start": v(18.27, 37.06) * mm, "end": v(17.6, 37.33) * mm});
            skArc(sketch, "E31.0.102", {"start": v(17.6, 37.33) * mm, "mid": v(15.99, 36.42) * mm, "end": v(14.58, 35.2) * mm});
            skLineSegment(sketch, "E31.0.103", {"start": v(14.58, 35.2) * mm, "end": v(13.37, 32.27) * mm});
            skArc(sketch, "E31.0.104", {"start": v(13.37, 32.27) * mm, "mid": v(11.23, 33.07) * mm, "end": v(9.04, 33.73) * mm});
            skLineSegment(sketch, "E31.0.105", {"start": v(9.04, 33.73) * mm, "end": v(9.86, 36.8) * mm});
            skArc(sketch, "E31.0.106", {"start": v(9.86, 36.8) * mm, "mid": v(9.49, 38.62) * mm, "end": v(8.77, 40.33) * mm});
            skLineSegment(sketch, "E31.0.107", {"start": v(8.77, 40.33) * mm, "end": v(8.06, 40.52) * mm});
            skLineSegment(sketch, "E31.0.108", {"start": v(8.06, 40.52) * mm, "end": v(7.34, 40.62) * mm});
            skArc(sketch, "E31.0.109", {"start": v(7.34, 40.62) * mm, "mid": v(6.02, 39.31) * mm, "end": v(4.97, 37.77) * mm});
            skLineSegment(sketch, "E31.0.110", {"start": v(4.97, 37.77) * mm, "end": v(4.56, 34.63) * mm});
            skArc(sketch, "E31.0.111", {"start": v(4.56, 34.63) * mm, "mid": v(2.28, 34.85) * mm, "end": v(0, 34.92) * mm});
            skLineSegment(sketch, "E31.0.112", {"start": v(0, 34.93) * mm, "end": v(0, 38.1) * mm});
            skArc(sketch, "E31.0.113", {"start": v(0, 38.1) * mm, "mid": v(-0.83, 39.76) * mm, "end": v(-1.97, 41.23) * mm});
            skLineSegment(sketch, "E31.0.114", {"start": v(-1.97, 41.23) * mm, "end": v(-2.7, 41.23) * mm});
            skLineSegment(sketch, "E31.0.115", {"start": v(-2.7, 41.23) * mm, "end": v(-3.43, 41.13) * mm});
            skArc(sketch, "E31.0.116", {"start": v(-3.43, 41.13) * mm, "mid": v(-4.36, 39.53) * mm, "end": v(-4.97, 37.77) * mm});
            skLineSegment(sketch, "E31.0.117", {"start": v(-4.97, 37.77) * mm, "end": v(-4.56, 34.63) * mm});
            skArc(sketch, "E31.0.118", {"start": v(-4.56, 34.63) * mm, "mid": v(-6.81, 34.25) * mm, "end": v(-9.04, 33.73) * mm});
            skLineSegment(sketch, "E31.0.119", {"start": v(-9.04, 33.73) * mm, "end": v(-9.86, 36.8) * mm});
            skArc(sketch, "E31.0.120", {"start": v(-9.86, 36.8) * mm, "mid": v(-11.1, 38.2) * mm, "end": v(-12.58, 39.31) * mm});
            skLineSegment(sketch, "E31.0.121", {"start": v(-12.58, 39.31) * mm, "end": v(-13.28, 39.12) * mm});
            skLineSegment(sketch, "E31.0.122", {"start": v(-13.28, 39.12) * mm, "end": v(-13.96, 38.84) * mm});
            skArc(sketch, "E31.0.123", {"start": v(-13.96, 38.84) * mm, "mid": v(-14.45, 37.05) * mm, "end": v(-14.58, 35.2) * mm});
            skLineSegment(sketch, "E31.0.124", {"start": v(-14.58, 35.2) * mm, "end": v(-13.37, 32.27) * mm});
            skArc(sketch, "E31.0.125", {"start": v(-13.37, 32.27) * mm, "mid": v(-15.45, 31.32) * mm, "end": v(-17.46, 30.25) * mm});
            skLineSegment(sketch, "E31.0.126", {"start": v(-17.46, 30.25) * mm, "end": v(-19.05, 33) * mm});
            skArc(sketch, "E31.0.127", {"start": v(-19.05, 33) * mm, "mid": v(-20.6, 34.02) * mm, "end": v(-22.32, 34.72) * mm});
            skLineSegment(sketch, "E31.0.128", {"start": v(-22.32, 34.72) * mm, "end": v(-22.95, 34.35) * mm});
            skLineSegment(sketch, "E31.0.129", {"start": v(-22.95, 34.35) * mm, "end": v(-23.53, 33.9) * mm});
            skArc(sketch, "E31.0.130", {"start": v(-23.53, 33.9) * mm, "mid": v(-23.54, 32.05) * mm, "end": v(-23.2, 30.23) * mm});
            skLineSegment(sketch, "E31.0.131", {"start": v(-23.2, 30.23) * mm, "end": v(-21.26, 27.7) * mm});
            skArc(sketch, "E31.0.132", {"start": v(-21.26, 27.7) * mm, "mid": v(-23.03, 26.26) * mm, "end": v(-24.7, 24.7) * mm});
            skLineSegment(sketch, "E31.0.133", {"start": v(-24.7, 24.7) * mm, "end": v(-26.94, 26.94) * mm});
            skArc(sketch, "E31.0.134", {"start": v(-26.94, 26.94) * mm, "mid": v(-28.7, 27.53) * mm, "end": v(-30.55, 27.76) * mm});
            skLineSegment(sketch, "E31.0.135", {"start": v(-30.55, 27.76) * mm, "end": v(-31.06, 27.24) * mm});
            skLineSegment(sketch, "E31.0.136", {"start": v(-31.06, 27.24) * mm, "end": v(-31.5, 26.66) * mm});
            skArc(sketch, "E31.0.137", {"start": v(-31.5, 26.66) * mm, "mid": v(-31.04, 24.87) * mm, "end": v(-30.23, 23.2) * mm});
            skLineSegment(sketch, "E31.0.138", {"start": v(-30.23, 23.2) * mm, "end": v(-27.7, 21.26) * mm});
            skArc(sketch, "E31.0.139", {"start": v(-27.7, 21.26) * mm, "mid": v(-29.04, 19.4) * mm, "end": v(-30.25, 17.46) * mm});
            skLineSegment(sketch, "E31.0.140", {"start": v(-30.25, 17.46) * mm, "end": v(-33, 19.05) * mm});
            skArc(sketch, "E31.0.141", {"start": v(-33, 19.05) * mm, "mid": v(-34.85, 19.16) * mm, "end": v(-36.7, 18.9) * mm});
            skLineSegment(sketch, "E31.0.142", {"start": v(-36.7, 18.9) * mm, "end": v(-37.06, 18.27) * mm});
            skLineSegment(sketch, "E31.0.143", {"start": v(-37.06, 18.27) * mm, "end": v(-37.33, 17.6) * mm});
            skArc(sketch, "E31.0.144", {"start": v(-37.33, 17.6) * mm, "mid": v(-36.42, 15.99) * mm, "end": v(-35.2, 14.58) * mm});
            skLineSegment(sketch, "E31.0.145", {"start": v(-35.2, 14.58) * mm, "end": v(-32.27, 13.37) * mm});
            skArc(sketch, "E31.0.146", {"start": v(-32.27, 13.37) * mm, "mid": v(-33.07, 11.23) * mm, "end": v(-33.73, 9.04) * mm});
            skLineSegment(sketch, "E31.0.147", {"start": v(-33.73, 9.04) * mm, "end": v(-36.8, 9.86) * mm});
            skArc(sketch, "E31.0.148", {"start": v(-36.8, 9.86) * mm, "mid": v(-38.62, 9.49) * mm, "end": v(-40.33, 8.77) * mm});
            skLineSegment(sketch, "E31.0.149", {"start": v(-40.33, 8.77) * mm, "end": v(-40.52, 8.06) * mm});
            skLineSegment(sketch, "E31.0.150", {"start": v(-40.52, 8.06) * mm, "end": v(-40.62, 7.34) * mm});
            skArc(sketch, "E31.0.151", {"start": v(-40.62, 7.34) * mm, "mid": v(-39.31, 6.02) * mm, "end": v(-37.77, 4.97) * mm});
            skLineSegment(sketch, "E31.0.152", {"start": v(-37.77, 4.97) * mm, "end": v(-34.63, 4.56) * mm});
            skArc(sketch, "E31.0.153", {"start": v(-34.63, 4.56) * mm, "mid": v(-34.85, 2.28) * mm, "end": v(-34.93, 0) * mm});
            skLineSegment(sketch, "E31.0.154", {"start": v(-34.93, 0) * mm, "end": v(-38.1, 0) * mm});
            skArc(sketch, "E31.0.155", {"start": v(-38.1, 0) * mm, "mid": v(-39.76, -0.83) * mm, "end": v(-41.23, -1.97) * mm});
            skLineSegment(sketch, "E31.0.156", {"start": v(-41.23, -1.97) * mm, "end": v(-41.23, -2.7) * mm});
            skLineSegment(sketch, "E31.0.157", {"start": v(-41.23, -2.7) * mm, "end": v(-41.13, -3.43) * mm});
            skArc(sketch, "E31.0.158", {"start": v(-41.13, -3.43) * mm, "mid": v(-39.53, -4.36) * mm, "end": v(-37.77, -4.97) * mm});
            skLineSegment(sketch, "E31.0.159", {"start": v(-37.77, -4.97) * mm, "end": v(-34.63, -4.56) * mm});
            skArc(sketch, "E31.0.160", {"start": v(-34.63, -4.56) * mm, "mid": v(-34.25, -6.81) * mm, "end": v(-33.73, -9.04) * mm});
            skLineSegment(sketch, "E31.0.161", {"start": v(-33.73, -9.04) * mm, "end": v(-36.8, -9.86) * mm});
            skArc(sketch, "E31.0.162", {"start": v(-36.8, -9.86) * mm, "mid": v(-38.2, -11.1) * mm, "end": v(-39.31, -12.58) * mm});
            skLineSegment(sketch, "E31.0.163", {"start": v(-39.31, -12.58) * mm, "end": v(-39.12, -13.28) * mm});
            skLineSegment(sketch, "E31.0.164", {"start": v(-39.12, -13.28) * mm, "end": v(-38.84, -13.96) * mm});
            skArc(sketch, "E31.0.165", {"start": v(-38.84, -13.96) * mm, "mid": v(-37.05, -14.45) * mm, "end": v(-35.2, -14.58) * mm});
            skLineSegment(sketch, "E31.0.166", {"start": v(-35.2, -14.58) * mm, "end": v(-32.27, -13.37) * mm});
            skArc(sketch, "E31.0.167", {"start": v(-32.27, -13.37) * mm, "mid": v(-31.32, -15.45) * mm, "end": v(-30.25, -17.46) * mm});
            skSolve(sketch);
        }
        {
            var Q0;
            Q0=makeQuery(id+"F0.imprint","IMPRINT",FACE,{"disambiguationData":[TD([[makeQuery(id+"F0.imprint","IMPRINT",EDGE,{"derivedFrom":sQuery(id+"F0.wireOp",EDGE,"E0")}),1.0]])]});
            var Q1;
            Q1=makeQuery(id+"F2.imprint","IMPRINT",FACE,{"disambiguationData":[TD([[makeQuery(id+"F2.imprint","IMPRINT",EDGE,{"derivedFrom":sQuery(id+"F2.wireOp",EDGE,"E31.0.0")}),1.0]])]});
            var Q2;
            Q2=sQuery(id+"F2.wireOp",VERTEX,"E31.0.115.start");
            var Q3;
            Q3=sQuery(id+"F0.wireOp",VERTEX,"E7.23.2.end");
            loft(context, id + "F3", {"sheetProfilesArray" : [{ "sheetProfileEntities" : qUnion([Q0]) }, { "sheetProfileEntities" : qUnion([Q1]) }], "matchConnections" : true, "connections" : [{ "connectionEntities" : qUnion([Q2, Q3]), "connectionEdgeQueries" : qUnion([]), "connectionEdgeParameters" : [] }]});
        }
        {
            var Q0;
            Q0=makeQuery(id+"F3.opLoft","CAP_FACE",FACE,{"disambiguationData":[OSD([makeQuery(id+"F2.imprint","IMPRINT",FACE,{"disambiguationData":[TD([[makeQuery(id+"F2.imprint","IMPRINT",EDGE,{"derivedFrom":sQuery(id+"F2.wireOp",EDGE,"E31.0.0")}),1.0]])]})])],"isStart":true});
            var sketch = newSketch(context, id + "F4", { "sketchPlane" : qUnion([Q0])});
            skCircle(sketch, "E32", {"center": v(0, 0) * mm, "radius": 6.35 * mm});
            skSolve(sketch);
        }
        {
            var Q0;
            Q0=makeQuery(id+"F4.imprint","IMPRINT",FACE,{"disambiguationData":[TD([[makeQuery(id+"F4.imprint","IMPRINT",EDGE,{"derivedFrom":sQuery(id+"F4.wireOp",EDGE,"E32")}),1.0]])]});
            extrude(context, id + "F5", {"entities" : qUnion([Q0]), "operationType" : NewBodyOperationType.REMOVE, "endBound" : BoundingType.THROUGH_ALL, "oppositeDirection" : true, "depth" : 25.4 * mm});
        }
    });
